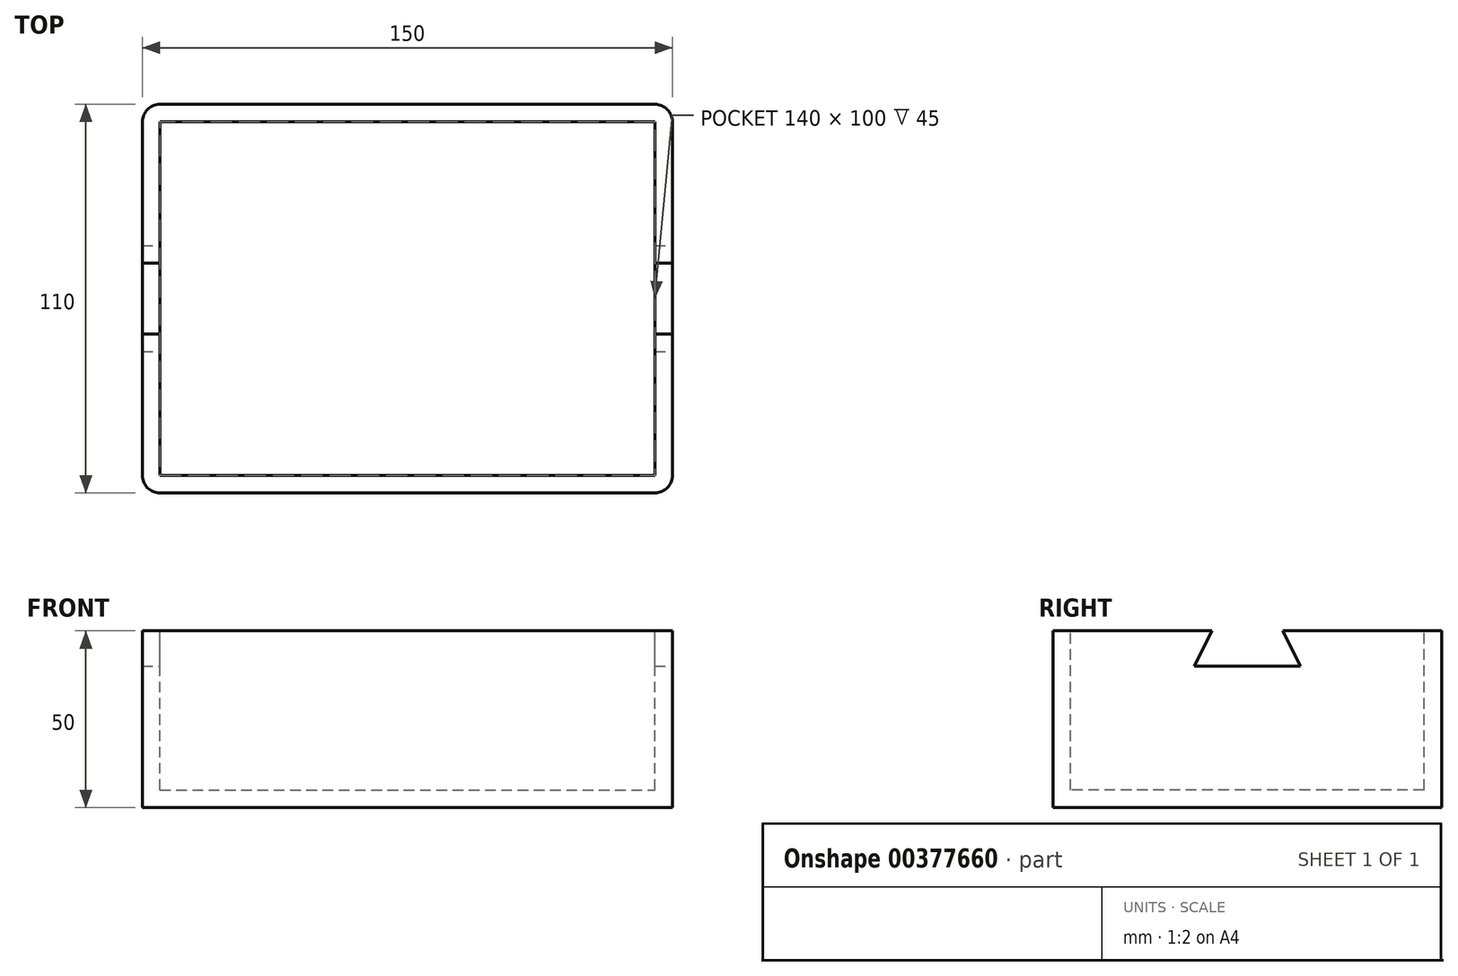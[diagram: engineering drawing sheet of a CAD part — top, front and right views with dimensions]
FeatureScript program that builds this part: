
annotation { "Feature Type Name" : "Feature", "Feature Type Description" : "" }
export const myFeature = defineFeature(function(context is Context, id is Id, definition is map)
    precondition{}
    {
        {
            var Q0;
            Q0=qCreatedBy(makeId("Top.planeOp"),FACE);
            var sketch = newSketch(context, id + "F0", { "sketchPlane" : qUnion([Q0])});
            skLineSegment(sketch, "E0.bottom", {"start": v(-75, 55) * mm, "end": v(75, 55) * mm});
            skLineSegment(sketch, "E0.top", {"start": v(-75, -55) * mm, "end": v(75, -55) * mm});
            skLineSegment(sketch, "E0.left", {"start": v(-75, 55) * mm, "end": v(-75, -55) * mm});
            skLineSegment(sketch, "E0.right", {"start": v(75, 55) * mm, "end": v(75, -55) * mm});
            skSolve(sketch);
        }
        {
            var Q0;
            Q0=makeQuery(id+"F0.imprint","IMPRINT",FACE,{"disambiguationData":[TD([[makeQuery(id+"F0.imprint","IMPRINT",EDGE,{"derivedFrom":sQuery(id+"F0.wireOp",EDGE,"E0.bottom")}),-1.0]])]});
            extrude(context, id + "F1", {"entities" : qUnion([Q0]), "depth" : 50 * mm});
        }
        {
            var Q0;
            Q0=makeQuery(id+"F1.opExtrude","CAP_FACE",FACE,{"disambiguationData":[OSD([sQuery(id+"F0.wireOp",EDGE,"E0.bottom"),sQuery(id+"F0.wireOp",EDGE,"E0.top"),sQuery(id+"F0.wireOp",EDGE,"E0.left"),sQuery(id+"F0.wireOp",EDGE,"E0.right")])],"isStart":false});
            var sketch = newSketch(context, id + "F2", { "sketchPlane" : qUnion([Q0])});
            skLineSegment(sketch, "E1.bottom", {"start": v(-70, 50) * mm, "end": v(70, 50) * mm});
            skLineSegment(sketch, "E1.top", {"start": v(-70, -50) * mm, "end": v(70, -50) * mm});
            skLineSegment(sketch, "E1.left", {"start": v(-70, 50) * mm, "end": v(-70, -50) * mm});
            skLineSegment(sketch, "E1.right", {"start": v(70, 50) * mm, "end": v(70, -50) * mm});
            skPoint(sketch, "E1.middle", {"position": v(0, 0) * mm});
            skSolve(sketch);
        }
        {
            var Q0;
            Q0=makeQuery(id+"F2.imprint","IMPRINT",FACE,{"disambiguationData":[TD([[makeQuery(id+"F2.imprint","IMPRINT",EDGE,{"derivedFrom":sQuery(id+"F2.wireOp",EDGE,"E1.bottom")}),-1.0]])]});
            extrude(context, id + "F3", {"entities" : qUnion([Q0]), "operationType" : NewBodyOperationType.REMOVE, "oppositeDirection" : true, "depth" : 45 * mm});
        }
        {
            var Q0;
            Q0=makeQuery(id+"F1.opExtrude","SWEPT_EDGE",EDGE,{"disambiguationData":[OSD([sQuery(id+"F0.wireOp",EDGE,"E0.top"),sQuery(id+"F0.wireOp",EDGE,"E0.right")])]});
            var Q1;
            Q1=makeQuery(id+"F1.opExtrude","SWEPT_EDGE",EDGE,{"disambiguationData":[OSD([sQuery(id+"F0.wireOp",EDGE,"E0.bottom"),sQuery(id+"F0.wireOp",EDGE,"E0.right")])]});
            var Q2;
            Q2=makeQuery(id+"F1.opExtrude","SWEPT_EDGE",EDGE,{"disambiguationData":[OSD([sQuery(id+"F0.wireOp",EDGE,"E0.bottom"),sQuery(id+"F0.wireOp",EDGE,"E0.left")])]});
            var Q3;
            Q3=makeQuery(id+"F1.opExtrude","SWEPT_EDGE",EDGE,{"disambiguationData":[OSD([sQuery(id+"F0.wireOp",EDGE,"E0.top"),sQuery(id+"F0.wireOp",EDGE,"E0.left")])]});
            fillet(context, id + "F4", {"entities" : qUnion([Q0, Q1, Q2, Q3]), "radius" : 5 * mm, "tangentPropagation" : true, "allowEdgeOverflow" : false});
        }
        {
            var Q0;
            Q0=makeQuery(id+"F1.opExtrude","SWEPT_FACE",FACE,{"disambiguationData":[OSD([sQuery(id+"F0.wireOp",EDGE,"E0.right")])]});
            var sketch = newSketch(context, id + "F5", { "sketchPlane" : qUnion([Q0])});
            skLineSegment(sketch, "E2", {"start": v(-10, 50) * mm, "end": v(10, 50) * mm});
            skLineSegment(sketch, "E3", {"start": v(10, 50) * mm, "end": v(15, 40) * mm});
            skLineSegment(sketch, "E4", {"start": v(15, 40) * mm, "end": v(-15, 40) * mm});
            skLineSegment(sketch, "E5", {"start": v(-15, 40) * mm, "end": v(-10, 50) * mm});
            skSolve(sketch);
        }
        {
            var Q0;
            Q0 = qSketchRegion(id + "F5", true);
            extrude(context, id + "F6", {"entities" : qUnion([Q0]), "operationType" : NewBodyOperationType.REMOVE, "oppositeDirection" : true, "depth" : 160 * mm});
        }
    });
